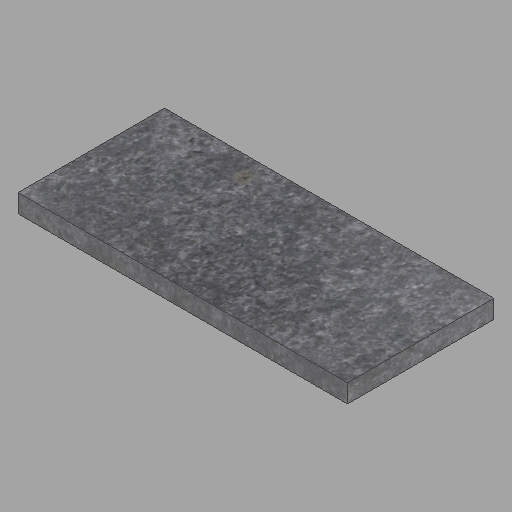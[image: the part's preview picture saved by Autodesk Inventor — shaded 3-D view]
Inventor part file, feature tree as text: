
AUTODESK INVENTOR PART (.ipt)
format: ipt  version: 2023 (Build 270158000, 158)  size: 226,304 bytes
history: native  units: in
note: dims shown in document units (in); Inventor stores cm internally (conversion verified against a paired STEP export)
features: other x1, extrude x1, sketch x1
ambient origin geometry x8: Origin, YZ Plane, XZ Plane, XY Plane, X Axis, Y Axis, Z Axis, Center Point
bodies: Solid1 (feature_tree)
feature tree (3):
  other  "2x16x36-3"
  extrude  "Extrusion1"  Depth=2.0in
  sketch  "Sketch1"  dims[d0=16.0in d1=2.0in d2=36.0in d3=0.0in]
